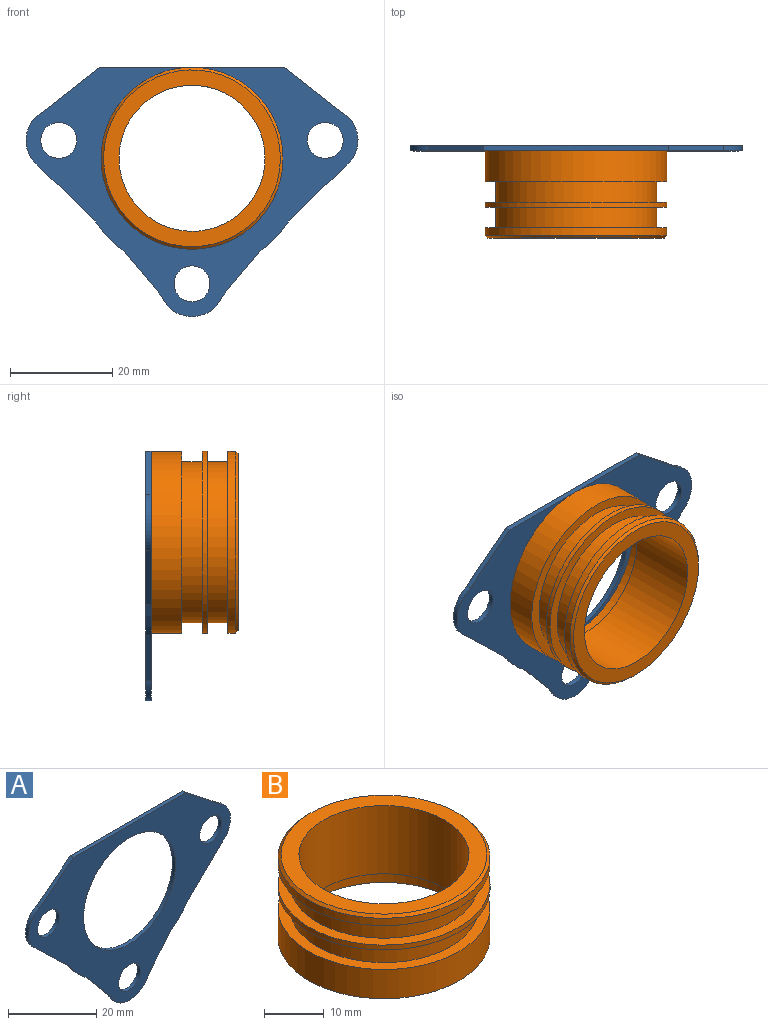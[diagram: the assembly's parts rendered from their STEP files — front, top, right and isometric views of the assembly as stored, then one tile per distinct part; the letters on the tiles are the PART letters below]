
ASSEMBLY  parts=2 mates=1
PART A: 18 faces, bbox 64.8x1x48.7 mm
  f0: plane 8.68x7.3mm, normal (0.77,0,-0.64), area 11.3mm2, adj f1,f14,f16,f17
  f1: cylinder r=22.5mm len=5.96mm, axis (0,1,0), area 8.3mm2, adj f0,f2,f16,f17
  f2: plane 10.99x10.64mm, normal (0.7,0,-0.72), area 15.3mm2, adj f1,f3,f16,f17
  f3: cylinder r=6.4mm len=10.87mm, axis (0,1,0), area 13.1mm2, adj f2,f4,f16,f17
  f4: plane 10.76x8.48mm, normal (0.62,0,0.79), area 13.7mm2, adj f3,f5,f16,f17
  f5: plane 36x1mm, normal (0,0,1), area 36mm2, adj f4,f6,f16,f17
  f6: plane 10.76x8.48mm, normal (-0.62,0,0.79), area 13.7mm2, adj f5,f7,f16,f17
  f7: cylinder r=6.4mm len=10.87mm, axis (0,1,0), area 13.1mm2, adj f6,f8,f16,f17
  f8: plane 10.99x10.64mm, normal (-0.7,0,-0.72), area 15.3mm2, adj f7,f9,f16,f17
  f9: cylinder r=22.5mm len=5.96mm, axis (0,1,0), area 8.3mm2, adj f8,f10,f16,f17
  f10: plane 8.68x7.3mm, normal (-0.77,0,-0.64), area 11.3mm2, adj f9,f14,f16,f17
  f11: cylinder r=3.5mm len=7mm, axis (0,1,0), area 22mm2, adj f16,f17
  f12: cylinder r=3.5mm len=7mm, axis (0,1,0), area 22mm2, adj f16,f17
  f13: cylinder r=3.5mm len=7mm, axis (0,1,0), area 22mm2, adj f16,f17
  f14: cylinder r=6.4mm len=11.89mm, axis (0,1,0), area 15.2mm2, adj f0,f10,f16,f17
  f15: cylinder r=14.75mm len=29.5mm, axis (0,1,0), area 92.7mm2, adj f16,f17
  f16: plane 64.8x48.65mm, normal (0,-1,0), area 1197.5mm2, adj f0,f1,f2,f3,f4,f5,f6,f7
  f17: plane 64.8x48.65mm, normal (0,1,0), area 1197.5mm2, adj f0,f1,f2,f3,f4,f5,f6,f7
PART B: 15 faces, bbox 35.5x35.5x17 mm
  f0: cylinder r=14.25mm len=28.5mm, axis (0,0,1), area 1253.5mm2, adj f3,f14
  f1: cylinder r=15.75mm len=31.5mm, axis (0,0,1), area 395.8mm2, adj f4,f6
  f2: cylinder r=17.75mm len=35.5mm, axis (0,0,-1), area 167.3mm2, adj f4,f11
  f3: plane 34.5x34.5mm, normal (0,0,1), area 296.9mm2, adj f0,f11
  f4: plane 35.5x35.5mm, normal (0,0,-1), area 210.5mm2, adj f1,f2
  f5: cylinder r=17.75mm len=35.5mm, axis (0,0,1), area 111.5mm2, adj f6,f10
  f6: plane 35.5x35.5mm, normal (0,0,1), area 210.5mm2, adj f1,f5
  f7: cylinder r=17.75mm len=35.5mm, axis (0,0,1), area 669.2mm2, adj f8,f12
  f8: plane 35.5x35.5mm, normal (0,0,1), area 210.5mm2, adj f7,f9
  f9: cylinder r=15.75mm len=31.5mm, axis (0,0,-1), area 395.8mm2, adj f8,f10
  f10: plane 35.5x35.5mm, normal (0,0,-1), area 210.5mm2, adj f5,f9
  f11: cone r=17.25mm half-angle=45deg, axis (0,0,-1), area 77.8mm2, adj f2,f3
  f12: plane 35.5x35.5mm, normal (0,0,-1), area 185.6mm2, adj f7,f13
  f13: cylinder r=16mm len=32mm, axis (0,0,-1), area 301.6mm2, adj f12,f14
  f14: plane 32x32mm, normal (0,0,-1), area 166.3mm2, adj f0,f13
PLACE A t=(40.79,-23.35,10.22)mm
PLACE B rot(axis=(1,0,0),90deg) t=(40.79,-39.35,10.22)mm
MATE fastened A.f9 <-> B.f2  axis (0,-1,0) through (40.79,-24.35,10.22)mm
